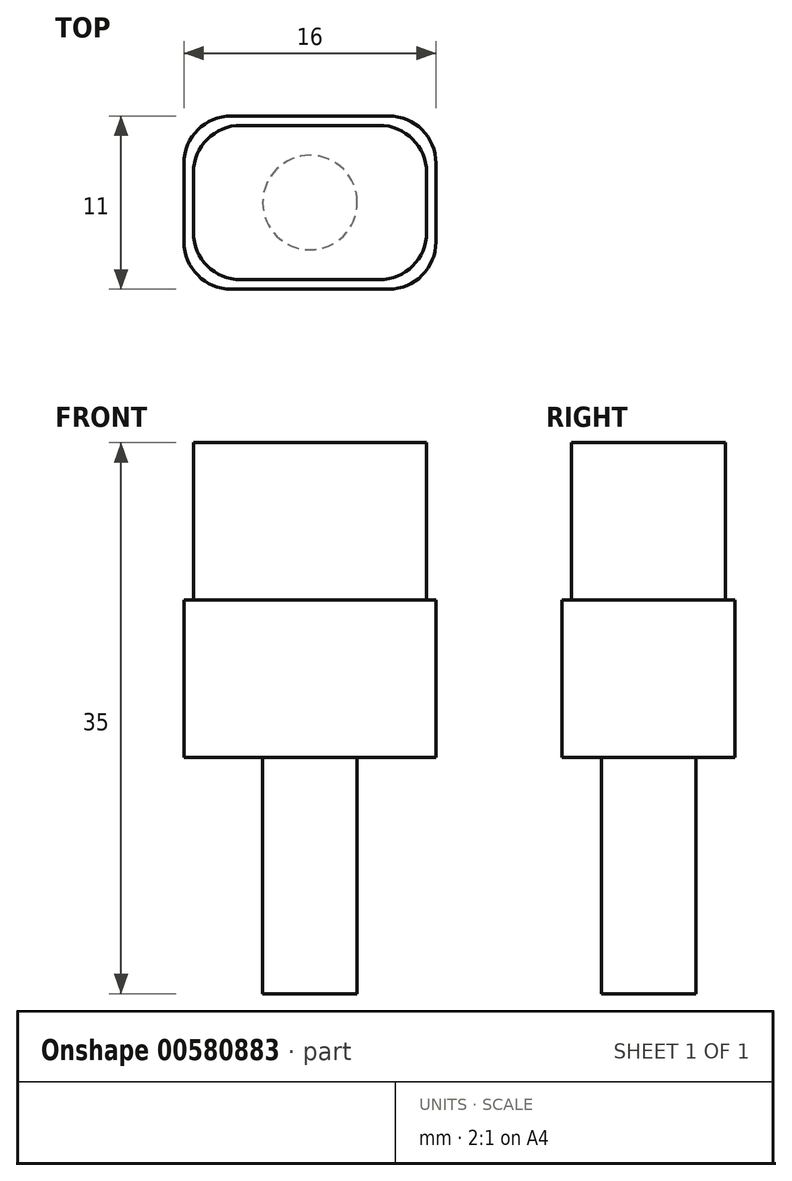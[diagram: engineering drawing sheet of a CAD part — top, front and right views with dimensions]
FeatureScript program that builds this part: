
annotation { "Feature Type Name" : "Feature", "Feature Type Description" : "" }
export const myFeature = defineFeature(function(context is Context, id is Id, definition is map)
    precondition{}
    {
        {
            var Q0;
            Q0=qCreatedBy(makeId("Top.planeOp"),FACE);
            var sketch = newSketch(context, id + "F0", { "sketchPlane" : qUnion([Q0])});
            skLineSegment(sketch, "E0.bottom", {"start": v(-5, 5.5) * mm, "end": v(5, 5.5) * mm});
            skLineSegment(sketch, "E0.top", {"start": v(-5, -5.5) * mm, "end": v(5, -5.5) * mm});
            skLineSegment(sketch, "E0.left", {"start": v(-8, 2.5) * mm, "end": v(-8, -2.5) * mm});
            skLineSegment(sketch, "E0.right", {"start": v(8, 2.5) * mm, "end": v(8, -2.5) * mm});
            skPoint(sketch, "E0.middle", {"position": v(0, 0) * mm});
            skPoint(sketch, "E1.visualSharp", {"position": v(8, 5.5) * mm});
            skArc(sketch, "E1.filletArc", {"start": v(8, 2.5) * mm, "mid": v(7.12, 4.62) * mm, "end": v(5, 5.5) * mm});
            skPoint(sketch, "E2.visualSharp", {"position": v(8, -5.5) * mm});
            skArc(sketch, "E2.filletArc", {"start": v(5, -5.5) * mm, "mid": v(7.12, -4.62) * mm, "end": v(8, -2.5) * mm});
            skPoint(sketch, "E3.visualSharp", {"position": v(-8, -5.5) * mm});
            skArc(sketch, "E3.filletArc", {"start": v(-8, -2.5) * mm, "mid": v(-7.12, -4.62) * mm, "end": v(-5, -5.5) * mm});
            skPoint(sketch, "E4.visualSharp", {"position": v(-8, 5.5) * mm});
            skArc(sketch, "E4.filletArc", {"start": v(-5, 5.5) * mm, "mid": v(-7.12, 4.62) * mm, "end": v(-8, 2.5) * mm});
            skSolve(sketch);
        }
        {
            var Q0;
            Q0=makeQuery(id+"F0.imprint","IMPRINT",FACE,{"disambiguationData":[TD([[makeQuery(id+"F0.imprint","IMPRINT",EDGE,{"derivedFrom":sQuery(id+"F0.wireOp",EDGE,"E0.bottom")}),-1.0]])]});
            extrude(context, id + "F1", {"entities" : qUnion([Q0]), "depth" : 10 * mm, "offsetDistance" : 25 * mm});
        }
        {
            var Q0;
            Q0=makeQuery(id+"F1.opExtrude","CAP_FACE",FACE,{"disambiguationData":[OSD([sQuery(id+"F0.wireOp",EDGE,"E0.bottom"),sQuery(id+"F0.wireOp",EDGE,"E0.top"),sQuery(id+"F0.wireOp",EDGE,"E0.left"),sQuery(id+"F0.wireOp",EDGE,"E0.right"),sQuery(id+"F0.wireOp",EDGE,"E1.filletArc"),sQuery(id+"F0.wireOp",EDGE,"E2.filletArc"),sQuery(id+"F0.wireOp",EDGE,"E3.filletArc"),sQuery(id+"F0.wireOp",EDGE,"E4.filletArc")])],"isStart":false});
            var sketch = newSketch(context, id + "F2", { "sketchPlane" : qUnion([Q0])});
            skLineSegment(sketch, "E5.bottom", {"start": v(-4.4, 4.9) * mm, "end": v(4.4, 4.9) * mm});
            skLineSegment(sketch, "E5.top", {"start": v(-4.4, -4.9) * mm, "end": v(4.4, -4.9) * mm});
            skLineSegment(sketch, "E5.left", {"start": v(-7.4, 1.9) * mm, "end": v(-7.4, -1.9) * mm});
            skLineSegment(sketch, "E5.right", {"start": v(7.4, 1.9) * mm, "end": v(7.4, -1.9) * mm});
            skPoint(sketch, "E5.middle", {"position": v(0, 0) * mm});
            skPoint(sketch, "E6.visualSharp", {"position": v(-7.4, 4.9) * mm});
            skArc(sketch, "E6.filletArc", {"start": v(-4.4, 4.9) * mm, "mid": v(-6.52, 4.02) * mm, "end": v(-7.4, 1.9) * mm});
            skPoint(sketch, "E7.visualSharp", {"position": v(-7.4, -4.9) * mm});
            skArc(sketch, "E7.filletArc", {"start": v(-7.4, -1.9) * mm, "mid": v(-6.52, -4.02) * mm, "end": v(-4.4, -4.9) * mm});
            skPoint(sketch, "E8.visualSharp", {"position": v(7.4, -4.9) * mm});
            skArc(sketch, "E8.filletArc", {"start": v(4.4, -4.9) * mm, "mid": v(6.52, -4.02) * mm, "end": v(7.4, -1.9) * mm});
            skPoint(sketch, "E9.visualSharp", {"position": v(7.4, 4.9) * mm});
            skArc(sketch, "E9.filletArc", {"start": v(7.4, 1.9) * mm, "mid": v(6.52, 4.02) * mm, "end": v(4.4, 4.9) * mm});
            skSolve(sketch);
        }
        {
            var Q0;
            Q0=makeQuery(id+"F2.imprint","IMPRINT",FACE,{"disambiguationData":[TD([[makeQuery(id+"F2.imprint","IMPRINT",EDGE,{"derivedFrom":sQuery(id+"F2.wireOp",EDGE,"E5.bottom")}),-1.0]])]});
            extrude(context, id + "F3", {"entities" : qUnion([Q0]), "operationType" : NewBodyOperationType.ADD, "depth" : 10 * mm, "offsetDistance" : 25 * mm});
        }
        {
            var Q0;
            Q0=makeQuery(id+"F1.opExtrude","CAP_FACE",FACE,{"disambiguationData":[OSD([sQuery(id+"F0.wireOp",EDGE,"E0.bottom"),sQuery(id+"F0.wireOp",EDGE,"E0.top"),sQuery(id+"F0.wireOp",EDGE,"E0.left"),sQuery(id+"F0.wireOp",EDGE,"E0.right"),sQuery(id+"F0.wireOp",EDGE,"E1.filletArc"),sQuery(id+"F0.wireOp",EDGE,"E2.filletArc"),sQuery(id+"F0.wireOp",EDGE,"E3.filletArc"),sQuery(id+"F0.wireOp",EDGE,"E4.filletArc")])],"isStart":true});
            var sketch = newSketch(context, id + "F4", { "sketchPlane" : qUnion([Q0])});
            skCircle(sketch, "E10", {"center": v(0, 0) * mm, "radius": 3 * mm});
            skSolve(sketch);
        }
        {
            var Q0;
            Q0=makeQuery(id+"F4.imprint","IMPRINT",FACE,{"disambiguationData":[TD([[makeQuery(id+"F4.imprint","IMPRINT",EDGE,{"derivedFrom":sQuery(id+"F4.wireOp",EDGE,"E10")}),1.0]])]});
            extrude(context, id + "F5", {"entities" : qUnion([Q0]), "operationType" : NewBodyOperationType.ADD, "depth" : 15 * mm, "offsetDistance" : 25 * mm});
        }
    });
